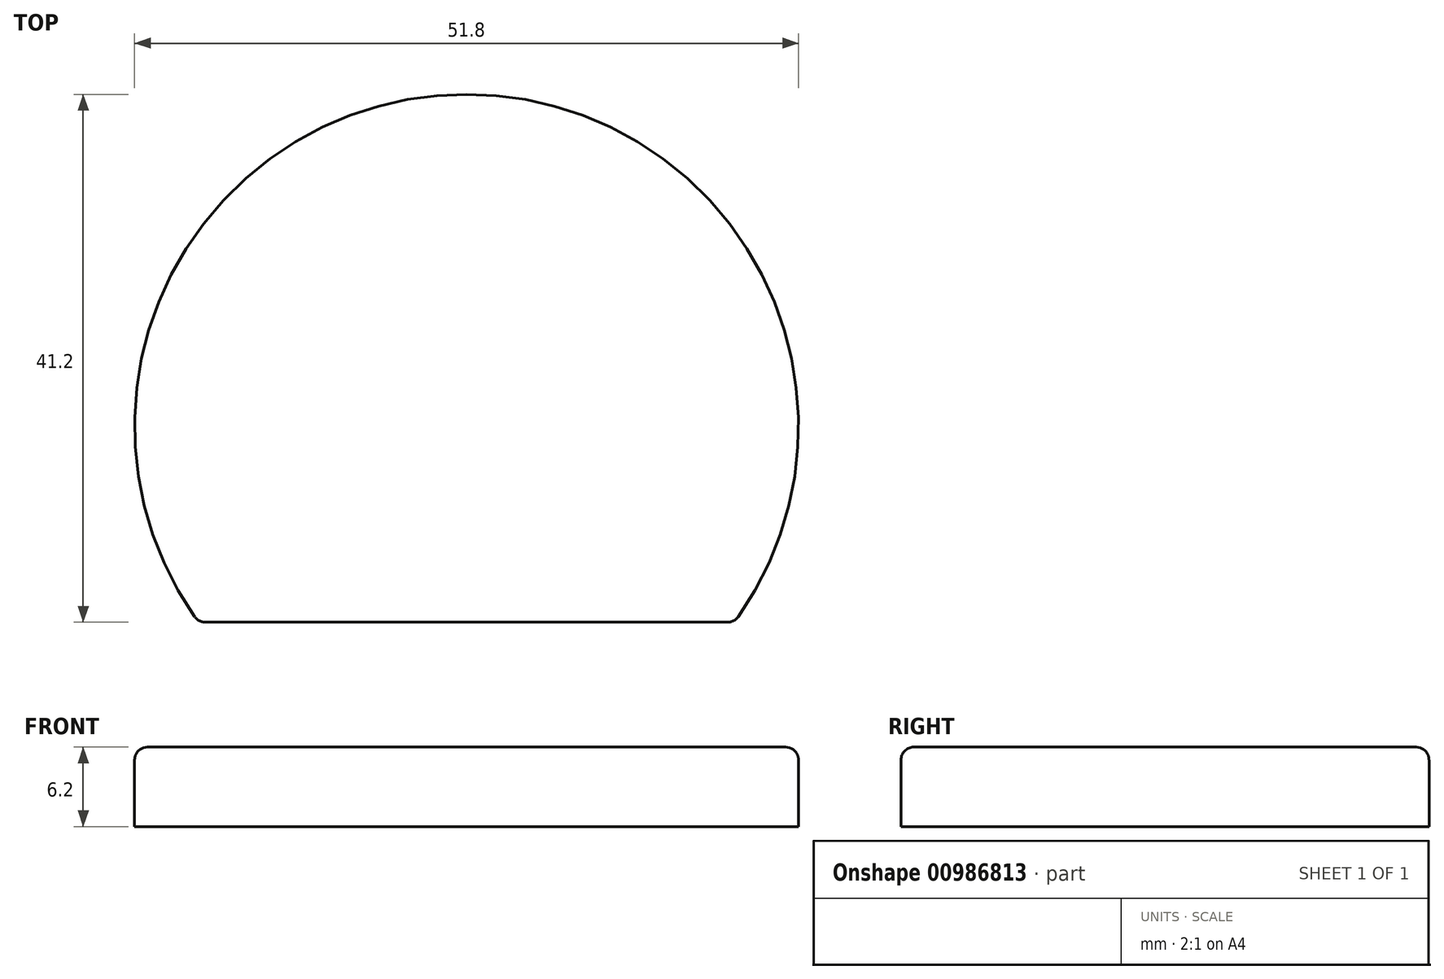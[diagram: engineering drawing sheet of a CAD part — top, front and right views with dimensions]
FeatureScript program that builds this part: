
annotation { "Feature Type Name" : "Feature", "Feature Type Description" : "" }
export const myFeature = defineFeature(function(context is Context, id is Id, definition is map)
    precondition{}
    {
        {
            var Q0;
            Q0=qCreatedBy(makeId("Top.planeOp"),FACE);
            var sketch = newSketch(context, id + "F0", { "sketchPlane" : qUnion([Q0])});
            skLineSegment(sketch, "E0", {"start": v(-20.9, -15.3) * mm, "end": v(20.9, -15.3) * mm});
            skLineSegment(sketch, "E1", {"start": v(0, -15.3) * mm, "end": v(0, 25.9) * mm, "construction": true});
            skArc(sketch, "E2", {"start": v(-20.9, -15.3) * mm, "mid": v(0, 25.9) * mm, "end": v(20.9, -15.3) * mm});
            skSolve(sketch);
        }
        {
            var Q0;
            Q0 = qSketchRegion(id + "F0", true);
            extrude(context, id + "F1", {"entities" : qUnion([Q0]), "depth" : 6.2 * mm, "offsetDistance" : 25 * mm});
        }
        {
            var Q0;
            {var subQ0=sQuery(id+"F0.wireOp",EDGE,"E2");var subQ1=sQuery(id+"F0.wireOp",EDGE,"E0");Q0=makeQuery(id+"F1.opExtrude","SWEPT_EDGE",EDGE,{"disambiguationData":[OSD([subQ1,subQ0]),TDD([makeQuery(id+"F0.imprint","INTERSECT",VERTEX,{"disambiguationData":[OD(1.0)],"derivedFrom":[subQ1,subQ0]})])]});}
            var Q1;
            Q1=makeQuery(id+"F1.opExtrude","CAP_EDGE",EDGE,{"disambiguationData":[OSD([sQuery(id+"F0.wireOp",EDGE,"E2")])],"isStart":false});
            var Q2;
            Q2=makeQuery(id+"F1.opExtrude","CAP_EDGE",EDGE,{"disambiguationData":[OSD([sQuery(id+"F0.wireOp",EDGE,"E0")])],"isStart":false});
            var Q3;
            {var subQ0=sQuery(id+"F0.wireOp",EDGE,"E2");var subQ1=sQuery(id+"F0.wireOp",EDGE,"E0");Q3=makeQuery(id+"F1.opExtrude","SWEPT_EDGE",EDGE,{"disambiguationData":[OSD([subQ1,subQ0]),TDD([makeQuery(id+"F0.imprint","INTERSECT",VERTEX,{"disambiguationData":[OD(0.0)],"derivedFrom":[subQ1,subQ0]})])]});}
            fillet(context, id + "F2", {"entities" : qUnion([Q0, Q1, Q2, Q3]), "radius" : 1 * mm, "tangentPropagation" : true, "allowEdgeOverflow" : false});
        }
    });
